# Revit family: EKF_EE_ШирокаяРейкаВертикальнаяTrivia_AVERES
name_source: partatom
category: Электрооборудование
units: mm (PartAtom-declared; Revit-internal decimal feet)

## family parameters
Всегда вертикально = Нет
На основе рабочей плоскости = Да
Общий = Да
При загрузке вырезать с полостями = Нет
Размер круглого соединителя = Использовать диаметр
Тип детали = Силовой щит
Точка расчета площади = Нет

## types (2) — shared parameters
ADSK_Единица измерения = шт.
ADSK_Завод-изготовитель = EKF
ADSK_Количество = 1
ADSK_Размер_Глубина = 42 мм
ADSK_Размер_Ширина = 78.2 мм
t2 = 2 мм
Вырез = 16 мм
Глубина = 42 мм
Изготовитель = EKF
Отступ = 4.6 мм
ОтступОтв = 24.5 мм
Серия номенклатуры = Averes
Степень защиты IP = -
ТВ = EKF_2_TRIVIA_AVERES
Тип установки = -
Шаг = 25 мм
Ширина = 78.2 мм
zero-valued in all types: ADSK_Масса, Отметка по умолчанию

## per-type parameters (varying)
| type | ADSK_Код изделия | ADSK_Марка | ADSK_Наименование | ADSK_Обозначение | ADSK_Размер_Высота | Высота | КоличествоКвОтверстий | КоличествоКрОтверстий | КоличествоКрСбоку | Тип |
| Широкая рейка вертикальная Д1900 (2шт) EKF AVERES | ARW19V | Широкая рейка вертикальная Д1900 (2 шт) EKF AVERES | Широкая рейка вертикальная Д1900 (2 шт) EKF AVERES | Широкая рейка вертикальная Д1900 (2 шт) EKF AVERES | 1924 мм | 1924 мм | 76 | 75 | 77 | 690 мм |
| Широкая рейка вертикальная Д1700 (2шт) EKF AVERES | ARW17V | Широкая рейка вертикальная Д1700 (2 шт) EKF AVERES | Широкая рейка вертикальная Д1700 (2 шт) EKF AVERES | Широкая рейка вертикальная Д1700 (2 шт) EKF AVERES | 1649 мм | 1649 мм | 65 | 64 | 66 | 689 мм |
